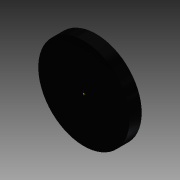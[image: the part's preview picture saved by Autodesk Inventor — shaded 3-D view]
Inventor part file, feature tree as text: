
AUTODESK INVENTOR PART (.ipt)
format: ipt  version: 2015 (Build 190159000, 159)  size: 86,528 bytes
history: native  units: in
note: dims shown in document units (in); Inventor stores cm internally (conversion verified against a paired STEP export)
features: sketch x2, extrude x1
ambient origin geometry x8: Origin, YZ Plane, XZ Plane, XY Plane, X Axis, Y Axis, Z Axis, Center Point
bodies: Solid1 (feature_tree)
feature tree (3):
  extrude  "Extrusion1"  Depth=0.0787in TaperAngle=0.0deg
  sketch  "Sketch2"
  sketch  "Sketch1"  dims[d0=0.5906in d1=0.0787in d2=0.0in]
